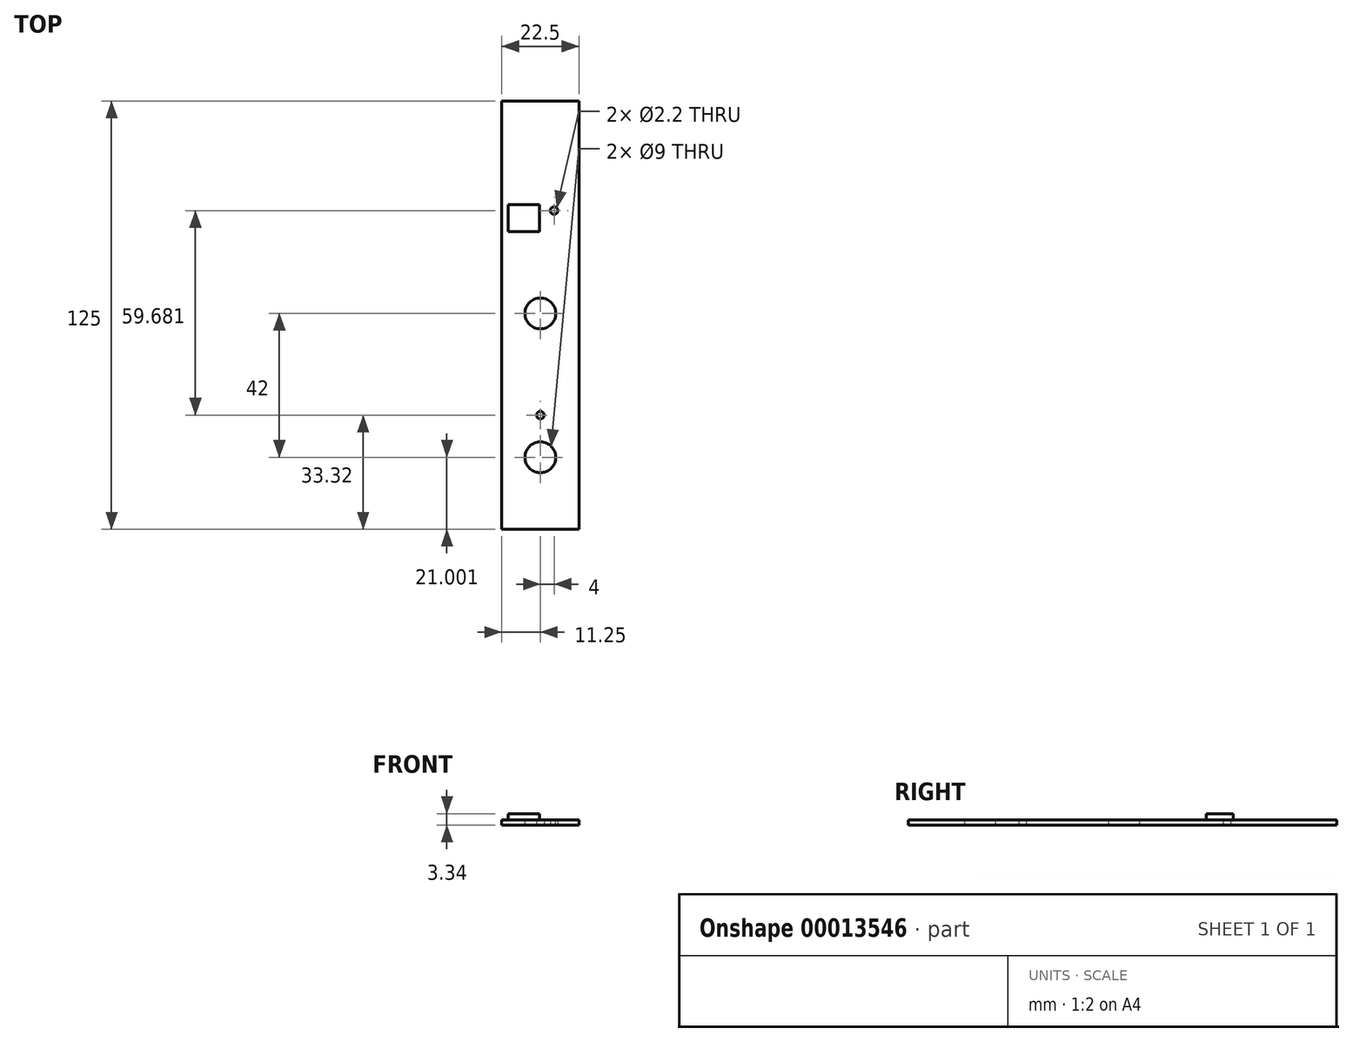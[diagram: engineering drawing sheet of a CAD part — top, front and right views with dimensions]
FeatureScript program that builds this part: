
annotation { "Feature Type Name" : "Feature", "Feature Type Description" : "" }
export const myFeature = defineFeature(function(context is Context, id is Id, definition is map)
    precondition{}
    {
        {
            var Q0;
            Q0=qCreatedBy(makeId("Top.planeOp"),FACE);
            var sketch = newSketch(context, id + "F0", { "sketchPlane" : qUnion([Q0])});
            skLineSegment(sketch, "E0", {"start": v(0, 0) * mm, "end": v(0, 128.85) * mm});
            skLineSegment(sketch, "E1", {"start": v(0, 128.85) * mm, "end": v(22.5, 128.85) * mm});
            skLineSegment(sketch, "E2", {"start": v(22.5, 128.85) * mm, "end": v(22.5, 0) * mm});
            skLineSegment(sketch, "E3", {"start": v(11.25, 128.85) * mm, "end": v(11.25, 0) * mm, "construction": true});
            skCircle(sketch, "E4", {"center": v(15.25, 96.85) * mm, "radius": 1.1 * mm});
            skLineSegment(sketch, "E5", {"start": v(22.5, 0) * mm, "end": v(0, 0) * mm, "construction": true});
            skCircle(sketch, "E6", {"center": v(11.25, 37.17) * mm, "radius": 1.1 * mm});
            skLineSegment(sketch, "E7", {"start": v(0, 3.85) * mm, "end": v(22.5, 3.85) * mm});
            skLineSegment(sketch, "E8", {"start": v(-2, 130.85) * mm, "end": v(24.5, 130.85) * mm, "construction": true});
            skLineSegment(sketch, "E9", {"start": v(24.5, 130.85) * mm, "end": v(24.5, 1.85) * mm, "construction": true});
            skLineSegment(sketch, "E10", {"start": v(24.5, 1.85) * mm, "end": v(-2, 1.85) * mm, "construction": true});
            skLineSegment(sketch, "E11", {"start": v(-2, 1.85) * mm, "end": v(-2, 130.85) * mm, "construction": true});
            skSolve(sketch);
        }
        {
            var Q0;
            Q0=qSketchRegion(id+"F0",true);
            extrude(context, id + "F1", {"entities" : qUnion([Q0]), "depth" : 1.57 * mm});
        }
        {
            var Q0;
            Q0=makeQuery(id+"F1.opExtrude","CAP_FACE",FACE,{"disambiguationData":[OSD([sQuery(id+"F0.wireOp",EDGE,"E0"),sQuery(id+"F0.wireOp",EDGE,"E1"),sQuery(id+"F0.wireOp",EDGE,"E2"),sQuery(id+"F0.wireOp",EDGE,"E4"),sQuery(id+"F0.wireOp",EDGE,"E6"),sQuery(id+"F0.wireOp",EDGE,"E7")])],"isStart":false});
            var sketch = newSketch(context, id + "F2", { "sketchPlane" : qUnion([Q0])});
            skLineSegment(sketch, "E12.rect.bottom", {"start": v(11.05, 90.75) * mm, "end": v(1.8, 90.75) * mm});
            skLineSegment(sketch, "E12.rect.top", {"start": v(11.05, 98.65) * mm, "end": v(1.8, 98.65) * mm});
            skLineSegment(sketch, "E12.rect.left", {"start": v(11.05, 90.75) * mm, "end": v(11.05, 98.65) * mm});
            skLineSegment(sketch, "E12.rect.right", {"start": v(1.8, 90.75) * mm, "end": v(1.8, 98.65) * mm});
            skPoint(sketch, "E12.rect.middle", {"position": v(6.43, 94.7) * mm});
            skSolve(sketch);
        }
        {
            var Q0;
            Q0 = qSketchRegion(id + "F2", true);
            extrude(context, id + "F3", {"entities" : qUnion([Q0]), "operationType" : NewBodyOperationType.ADD, "depth" : 1.77 * mm});
        }
        {
            var Q0;
            Q0=makeQuery(id+"F1.opExtrude","CAP_FACE",FACE,{"disambiguationData":[OSD([sQuery(id+"F0.wireOp",EDGE,"E0"),sQuery(id+"F0.wireOp",EDGE,"E1"),sQuery(id+"F0.wireOp",EDGE,"E2"),sQuery(id+"F0.wireOp",EDGE,"E4"),sQuery(id+"F0.wireOp",EDGE,"E6"),sQuery(id+"F0.wireOp",EDGE,"E7")])],"isStart":false});
            var sketch = newSketch(context, id + "F4", { "sketchPlane" : qUnion([Q0])});
            skLineSegment(sketch, "E13.bottom", {"start": v(0, 128.85) * mm, "end": v(22.5, 128.85) * mm});
            skLineSegment(sketch, "E13.left", {"start": v(0, 128.85) * mm, "end": v(0, 3.85) * mm, "construction": true});
            skLineSegment(sketch, "E13.right", {"start": v(22.5, 128.85) * mm, "end": v(22.5, 3.85) * mm, "construction": true});
            skLineSegment(sketch, "E14", {"start": v(0, 81.34) * mm, "end": v(22.5, 81.34) * mm, "construction": true});
            skSolve(sketch);
        }
        {
            var Q0;
            Q0=makeQuery(id+"F4.imprint","IMPRINT",FACE,{"disambiguationData":[TD([[makeQuery(id+"F4.imprint","IMPRINT",EDGE,{"derivedFrom":sQuery(id+"F4.wireOp",EDGE,"E13.bottom")}),-1.0]])]});
            var sketch = newSketch(context, id + "F5", { "sketchPlane" : qUnion([Q0])});
            skLineSegment(sketch, "E15", {"start": v(11.25, 128.85) * mm, "end": v(11.25, 1.85) * mm, "construction": true});
            skCircle(sketch, "E16", {"center": v(11.25, 66.85) * mm, "radius": 4.5 * mm});
            skCircle(sketch, "E17", {"center": v(11.25, 24.85) * mm, "radius": 4.5 * mm});
            skLineSegment(sketch, "E18.rect.top", {"start": v(24.5, 130.85) * mm, "end": v(-2, 130.85) * mm, "construction": true});
            skLineSegment(sketch, "E18.rect.left", {"start": v(24.5, 1.85) * mm, "end": v(24.5, 130.85) * mm, "construction": true});
            skLineSegment(sketch, "E18.rect.right", {"start": v(-2, 1.85) * mm, "end": v(-2, 130.85) * mm, "construction": true});
            skPoint(sketch, "E18.rect.middle", {"position": v(11.25, 66.35) * mm});
            skCircle(sketch, "E19", {"center": v(11.25, 45.85) * mm, "radius": 7.5 * mm, "construction": true});
            skLineSegment(sketch, "E20", {"start": v(24.5, 1.85) * mm, "end": v(-2, 1.85) * mm, "construction": true});
            skLineSegment(sketch, "E21", {"start": v(11.25, 66.85) * mm, "end": v(11.25, 45.85) * mm, "construction": true});
            skLineSegment(sketch, "E22", {"start": v(11.25, 45.85) * mm, "end": v(11.25, 24.85) * mm, "construction": true});
            skSolve(sketch);
        }
        {
            var Q0;
            Q0 = qSketchRegion(id + "F5", true);
            var Q1;
            Q1=makeQuery(id+"F1.opExtrude","CAP_FACE",FACE,{"disambiguationData":[OSD([sQuery(id+"F0.wireOp",EDGE,"E0"),sQuery(id+"F0.wireOp",EDGE,"E1"),sQuery(id+"F0.wireOp",EDGE,"E2"),sQuery(id+"F0.wireOp",EDGE,"E4"),sQuery(id+"F0.wireOp",EDGE,"E6"),sQuery(id+"F0.wireOp",EDGE,"E7")])],"isStart":true});
            extrude(context, id + "F6", {"entities" : qUnion([Q0]), "operationType" : NewBodyOperationType.REMOVE, "endBound" : BoundingType.UP_TO_SURFACE, "oppositeDirection" : true, "endBoundEntityFace" : qUnion([Q1]), "depth" : 25 * mm});
        }
    });
